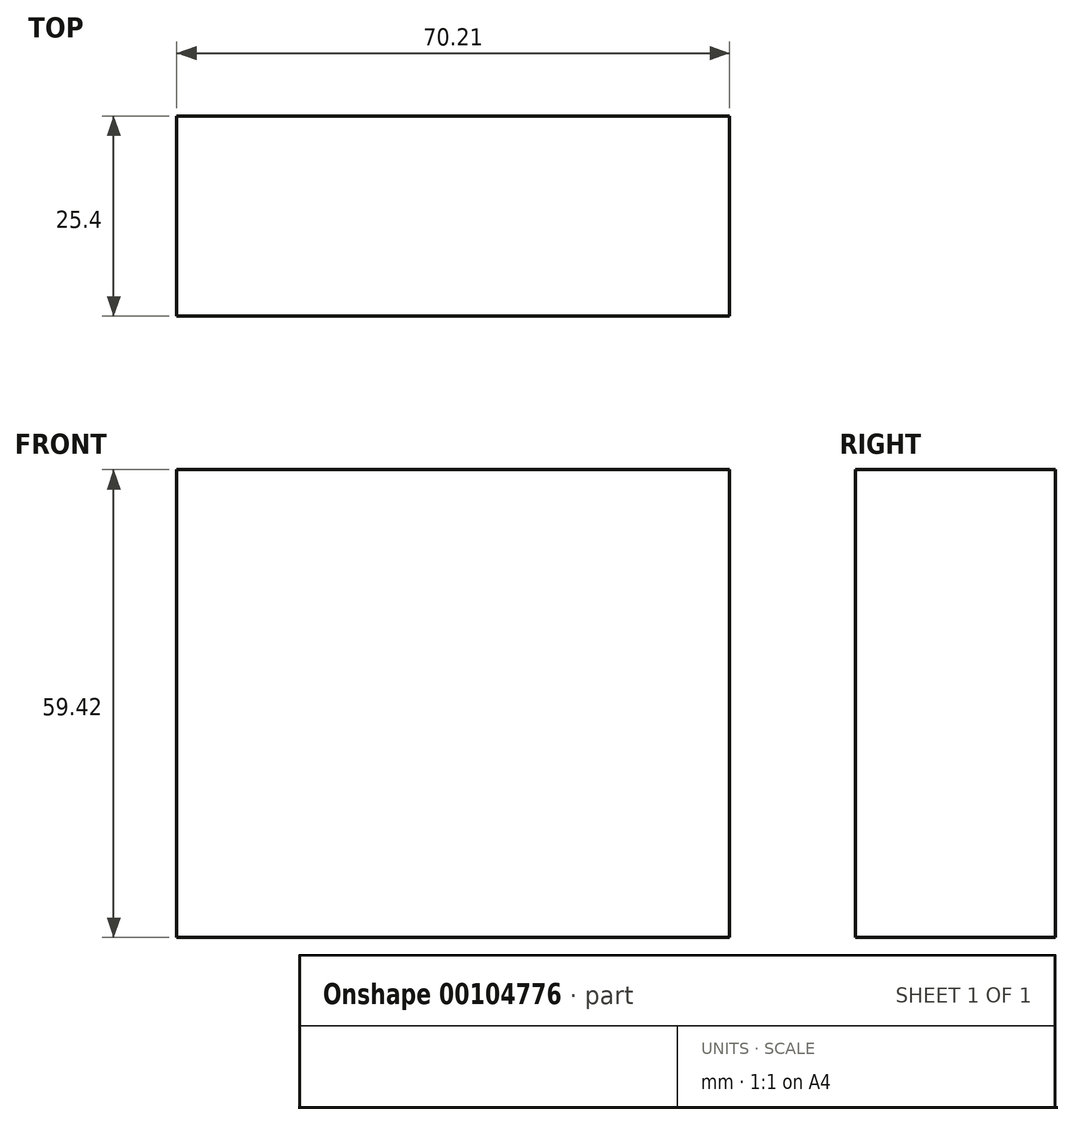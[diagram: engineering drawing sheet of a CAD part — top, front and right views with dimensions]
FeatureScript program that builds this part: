
annotation { "Feature Type Name" : "Feature", "Feature Type Description" : "" }
export const myFeature = defineFeature(function(context is Context, id is Id, definition is map)
    precondition{}
    {
        {
            var Q0;
            Q0=qCreatedBy(makeId("Front.planeOp"),FACE);
            var sketch = newSketch(context, id + "F0", { "sketchPlane" : qUnion([Q0])});
            skLineSegment(sketch, "E0.bottom", {"start": v(70.2, 59.42) * mm, "end": v(0, 59.42) * mm});
            skLineSegment(sketch, "E0.top", {"start": v(70.2, 0) * mm, "end": v(0, 0) * mm});
            skLineSegment(sketch, "E0.left", {"start": v(70.2, 59.42) * mm, "end": v(70.2, 0) * mm});
            skLineSegment(sketch, "E0.right", {"start": v(0, 59.42) * mm, "end": v(0, 0) * mm});
            skSolve(sketch);
        }
        {
            var Q0;
            Q0 = qSketchRegion(id + "F0", true);
            var sketch = newSketch(context, id + "F1", { "sketchPlane" : qUnion([Q0])});
            skArc(sketch, "E1", {"start": v(40.96, 44.99) * mm, "mid": v(18.22, 52.83) * mm, "end": v(25.45, 29.89) * mm});
            skLineSegment(sketch, "E2", {"start": v(40.96, 44.99) * mm, "end": v(25.45, 29.89) * mm});
            skSolve(sketch);
        }
        {
            var Q0;
            Q0 = qSketchRegion(id + "F0", true);
            extrude(context, id + "F2", {"entities" : qUnion([Q0]), "depth" : 25.4 * mm});
        }
        {
            var Q0;
            Q0=makeQuery(id+"F1.imprint","IMPRINT",FACE,{"disambiguationData":[TD([[makeQuery(id+"F1.imprint","IMPRINT",EDGE,{"derivedFrom":sQuery(id+"F1.wireOp",EDGE,"E1")}),1.0]])]});
            var Q1;
            Q1=makeQuery(id+"F1.imprint","IMPRINT",FACE,{"disambiguationData":[TD([[makeQuery(id+"F1.imprint","IMPRINT",EDGE,{"derivedFrom":sQuery(id+"F1.wireOp",EDGE,"E1")}),1.0]])]});
            extrude(context, id + "F3", {"entities" : qUnion([Q0, Q1]), "operationType" : NewBodyOperationType.ADD, "depth" : 12.96 * mm});
        }
        {
            var Q0;
            Q0=sQuery(id+"F1.wireOp",EDGE,"E1");
            var Q1;
            Q1 = qBodyType(qCreatedBy(id + "F1" ,EDGE), BodyType.WIRE);
            var Q2;
            Q2=sQuery(id+"F1.wireOp",EDGE,"E2");
            extrude(context, id + "F4", {"bodyType" : ToolBodyType.SURFACE, "surfaceEntities" : qUnion([Q0, Q1, Q2]), "depth" : 25.4 * mm, "hasSecondDirection" : true, "secondDirectionOppositeDirection" : true, "secondDirectionDepth" : 25.4 * mm});
        }
    });
